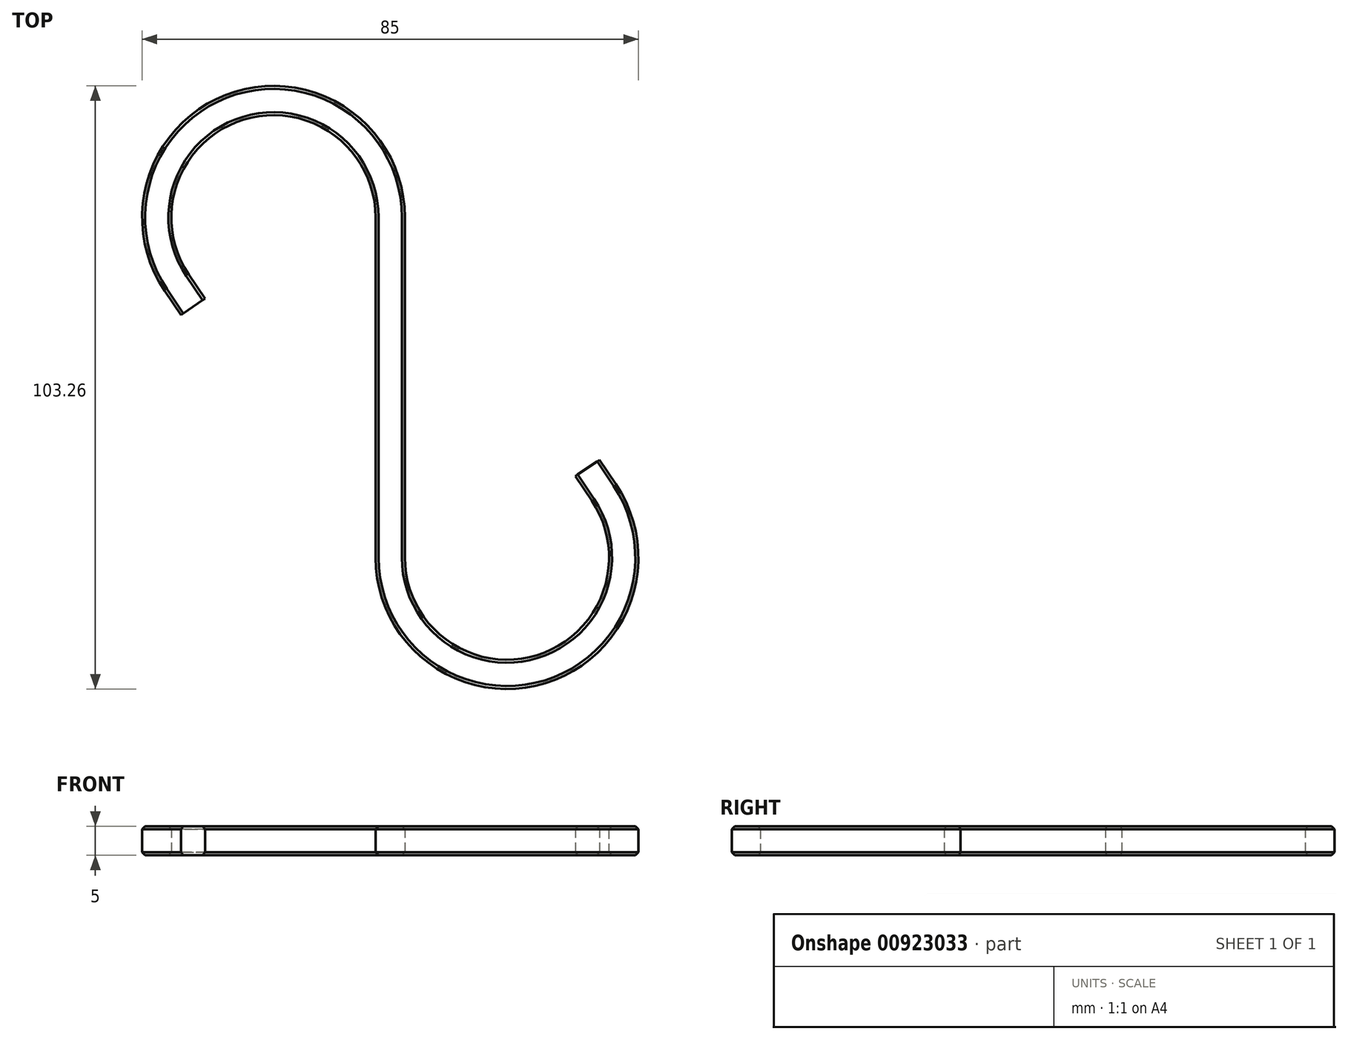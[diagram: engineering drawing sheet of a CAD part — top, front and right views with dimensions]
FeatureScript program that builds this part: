
annotation { "Feature Type Name" : "Feature", "Feature Type Description" : "" }
export const myFeature = defineFeature(function(context is Context, id is Id, definition is map)
    precondition{}
    {
        {
            var Q0;
            Q0=qCreatedBy(makeId("Top.planeOp"),FACE);
            var sketch = newSketch(context, id + "F0", { "sketchPlane" : qUnion([Q0])});
            skLineSegment(sketch, "E0", {"start": v(0, 29.13) * mm, "end": v(0, -29.13) * mm});
            skLineSegment(sketch, "E1", {"start": v(0, 29.13) * mm, "end": v(-44.31, 29.13) * mm, "construction": true});
            skLineSegment(sketch, "E2", {"start": v(0, 29.13) * mm, "end": v(-36.58, 17.95) * mm, "construction": true});
            skArc(sketch, "E3", {"start": v(0, 29.13) * mm, "mid": v(-25.85, 48.26) * mm, "end": v(-36.58, 17.95) * mm});
            skLineSegment(sketch, "E4", {"start": v(-36.58, 17.95) * mm, "end": v(-33.78, 13.8) * mm});
            skLineSegment(sketch, "E5", {"start": v(0, -29.13) * mm, "end": v(47.71, -29.13) * mm, "construction": true});
            skLineSegment(sketch, "E6", {"start": v(0, -29.13) * mm, "end": v(42.9, -16.02) * mm, "construction": true});
            skArc(sketch, "E7", {"start": v(0, -29.13) * mm, "mid": v(25.85, -48.26) * mm, "end": v(36.58, -17.95) * mm});
            skLineSegment(sketch, "E8", {"start": v(36.58, -17.95) * mm, "end": v(33.78, -13.8) * mm});
            skSolve(sketch);
        }
        {
            var Q0;
            Q0=qCreatedBy(makeId("Front.planeOp"),FACE);
            var sketch = newSketch(context, id + "F1", { "sketchPlane" : qUnion([Q0])});
            skLineSegment(sketch, "E9.bottom", {"start": v(2.5, 2.5) * mm, "end": v(-2.5, 2.5) * mm});
            skLineSegment(sketch, "E9.top", {"start": v(2.5, -2.5) * mm, "end": v(-2.5, -2.5) * mm});
            skLineSegment(sketch, "E9.left", {"start": v(2.5, 2.5) * mm, "end": v(2.5, -2.5) * mm});
            skLineSegment(sketch, "E9.right", {"start": v(-2.5, 2.5) * mm, "end": v(-2.5, -2.5) * mm});
            skPoint(sketch, "E9.middle", {"position": v(0, 0) * mm});
            skSolve(sketch);
        }
        {
            var Q0;
            Q0=makeQuery(id+"F1.imprint","IMPRINT",FACE,{"disambiguationData":[TD([[makeQuery(id+"F1.imprint","IMPRINT",EDGE,{"derivedFrom":sQuery(id+"F1.wireOp",EDGE,"E9.bottom")}),1.0]])]});
            var Q1;
            Q1=sQuery(id+"F0.wireOp",EDGE,"E0");
            var Q2;
            Q2=sQuery(id+"F0.wireOp",EDGE,"E7");
            var Q3;
            Q3=sQuery(id+"F0.wireOp",EDGE,"E8");
            var Q4;
            Q4=sQuery(id+"F0.wireOp",EDGE,"E3");
            var Q5;
            Q5=sQuery(id+"F0.wireOp",EDGE,"E4");
            sweep(context, id + "F2", {"profiles" : qUnion([Q0]), "path" : qUnion([Q1, Q2, Q3, Q4, Q5])});
        }
        {
            var Q0;
            Q0=makeQuery(id+"F2.opSweep","SWEPT_EDGE",EDGE,{"disambiguationData":[OSD([sQuery(id+"F0.wireOp",EDGE,"E0"),sQuery(id+"F1.wireOp",EDGE,"E9.top"),sQuery(id+"F1.wireOp",EDGE,"E9.right")])]});
            var Q1;
            Q1=makeQuery(id+"F2.opSweep","SWEPT_EDGE",EDGE,{"disambiguationData":[OSD([sQuery(id+"F0.wireOp",EDGE,"E3"),sQuery(id+"F1.wireOp",EDGE,"E9.top"),sQuery(id+"F1.wireOp",EDGE,"E9.left")])]});
            var Q2;
            Q2=makeQuery(id+"F2.opSweep","SWEPT_EDGE",EDGE,{"disambiguationData":[OSD([sQuery(id+"F0.wireOp",EDGE,"E3"),sQuery(id+"F1.wireOp",EDGE,"E9.bottom"),sQuery(id+"F1.wireOp",EDGE,"E9.left")])]});
            var Q3;
            Q3=makeQuery(id+"F2.opSweep","SWEPT_EDGE",EDGE,{"disambiguationData":[OSD([sQuery(id+"F0.wireOp",EDGE,"E0"),sQuery(id+"F1.wireOp",EDGE,"E9.bottom"),sQuery(id+"F1.wireOp",EDGE,"E9.right")])]});
            chamfer(context, id + "F3", {"entities" : qUnion([Q0, Q1, Q2, Q3]), "width" : 0.5 * mm, "tangentPropagation" : true});
        }
    });
